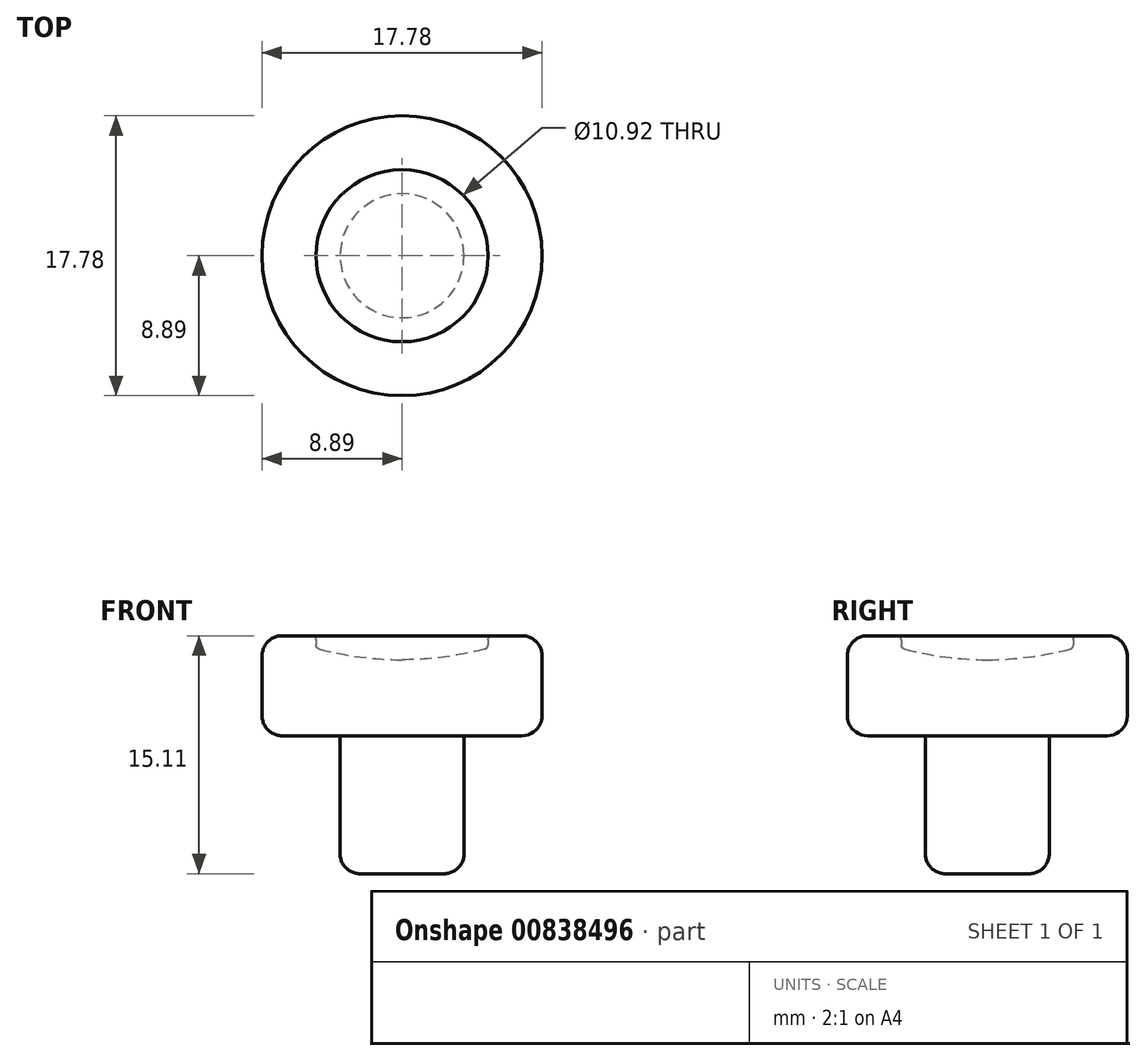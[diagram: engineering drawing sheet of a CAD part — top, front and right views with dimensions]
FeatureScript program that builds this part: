
annotation { "Feature Type Name" : "Feature", "Feature Type Description" : "" }
export const myFeature = defineFeature(function(context is Context, id is Id, definition is map)
    precondition{}
    {
        {
            var Q0;
            Q0=qCreatedBy(makeId("Front.planeOp"),FACE);
            var sketch = newSketch(context, id + "F0", { "sketchPlane" : qUnion([Q0])});
            skLineSegment(sketch, "E0", {"start": v(0, 0) * mm, "end": v(3.94, 0) * mm});
            skLineSegment(sketch, "E1", {"start": v(3.94, 0) * mm, "end": v(3.94, 8.76) * mm});
            skLineSegment(sketch, "E2", {"start": v(3.94, 8.76) * mm, "end": v(8.9, 8.76) * mm});
            skLineSegment(sketch, "E3", {"start": v(8.9, 8.76) * mm, "end": v(8.9, 15.11) * mm});
            skArc(sketch, "E4", {"start": v(0, 13.59) * mm, "mid": v(2.76, 13.77) * mm, "end": v(5.46, 14.33) * mm});
            skLineSegment(sketch, "E5", {"start": v(0, 0) * mm, "end": v(0, 13.59) * mm});
            skLineSegment(sketch, "E6", {"start": v(5.46, 14.33) * mm, "end": v(5.46, 15.11) * mm});
            skLineSegment(sketch, "E7", {"start": v(5.46, 15.11) * mm, "end": v(8.9, 15.11) * mm});
            skSolve(sketch);
        }
        {
            var Q0;
            Q0=makeQuery(id+"F0.imprint","IMPRINT",FACE,{"disambiguationData":[TD([[makeQuery(id+"F0.imprint","IMPRINT",EDGE,{"derivedFrom":sQuery(id+"F0.wireOp",EDGE,"E0")}),1.0]])]});
            var Q1;
            Q1=sQuery(id+"F0.wireOp",EDGE,"E5");
            revolve(context, id + "F1", {"surfaceOperationType" : NewSurfaceOperationType.NEW, "entities" : qUnion([Q0]), "axis" : qUnion([Q1]), "revolveType" : RevolveType.FULL});
        }
        {
            var Q0;
            Q0=makeQuery(id+"F1.opRevolve","SWEPT_EDGE",EDGE,{"disambiguationData":[OSD([sQuery(id+"F0.wireOp",EDGE,"E4"),sQuery(id+"F0.wireOp",EDGE,"E6")])]});
            fillet(context, id + "F2", {"entities" : qUnion([Q0]), "radius" : 0.25 * mm, "tangentPropagation" : true, "allowEdgeOverflow" : false});
        }
        {
            var Q0;
            Q0=makeQuery(id+"F1.opRevolve","SWEPT_EDGE",EDGE,{"disambiguationData":[OSD([sQuery(id+"F0.wireOp",EDGE,"E3"),sQuery(id+"F0.wireOp",EDGE,"E7")])]});
            var Q1;
            Q1=makeQuery(id+"F1.opRevolve","SWEPT_EDGE",EDGE,{"disambiguationData":[OSD([sQuery(id+"F0.wireOp",EDGE,"E2"),sQuery(id+"F0.wireOp",EDGE,"E3")])]});
            var Q2;
            Q2=makeQuery(id+"F1.opRevolve","SWEPT_EDGE",EDGE,{"disambiguationData":[OSD([sQuery(id+"F0.wireOp",EDGE,"E0"),sQuery(id+"F0.wireOp",EDGE,"E1")])]});
            fillet(context, id + "F3", {"entities" : qUnion([Q0, Q1, Q2]), "radius" : 1.27 * mm, "tangentPropagation" : true, "allowEdgeOverflow" : false});
        }
        {
            var Q0;
            Q0=makeQuery(id+"F1.opRevolve","SWEPT_EDGE",EDGE,{"disambiguationData":[OSD([sQuery(id+"F0.wireOp",EDGE,"E6"),sQuery(id+"F0.wireOp",EDGE,"E7")])]});
            fillet(context, id + "F4", {"entities" : qUnion([Q0]), "radius" : 0.25 * mm, "tangentPropagation" : true, "allowEdgeOverflow" : false});
        }
    });
